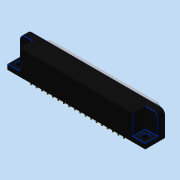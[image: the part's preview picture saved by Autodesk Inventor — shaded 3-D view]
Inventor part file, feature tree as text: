
AUTODESK INVENTOR PART (.ipt)
format: ipt  version: 2016 (Build 200138000, 138)  size: 330,240 bytes
history: native  units: in
note: dims shown in document units (in); Inventor stores cm internally (conversion verified against a paired STEP export)
features: fillet x1
ambient origin geometry x8: Origin, YZ Plane, XZ Plane, XY Plane, X Axis, Y Axis, Z Axis, Center Point
bodies: Solid1 (feature_tree)
feature tree (1):
  fillet  "Fillet2"  [1 undecoded]
note: 1 required parameter value undecoded (feature->parameter linkage not recoverable at this tier; creation-order binding heuristic only, values carry confidence <= 0.55)
